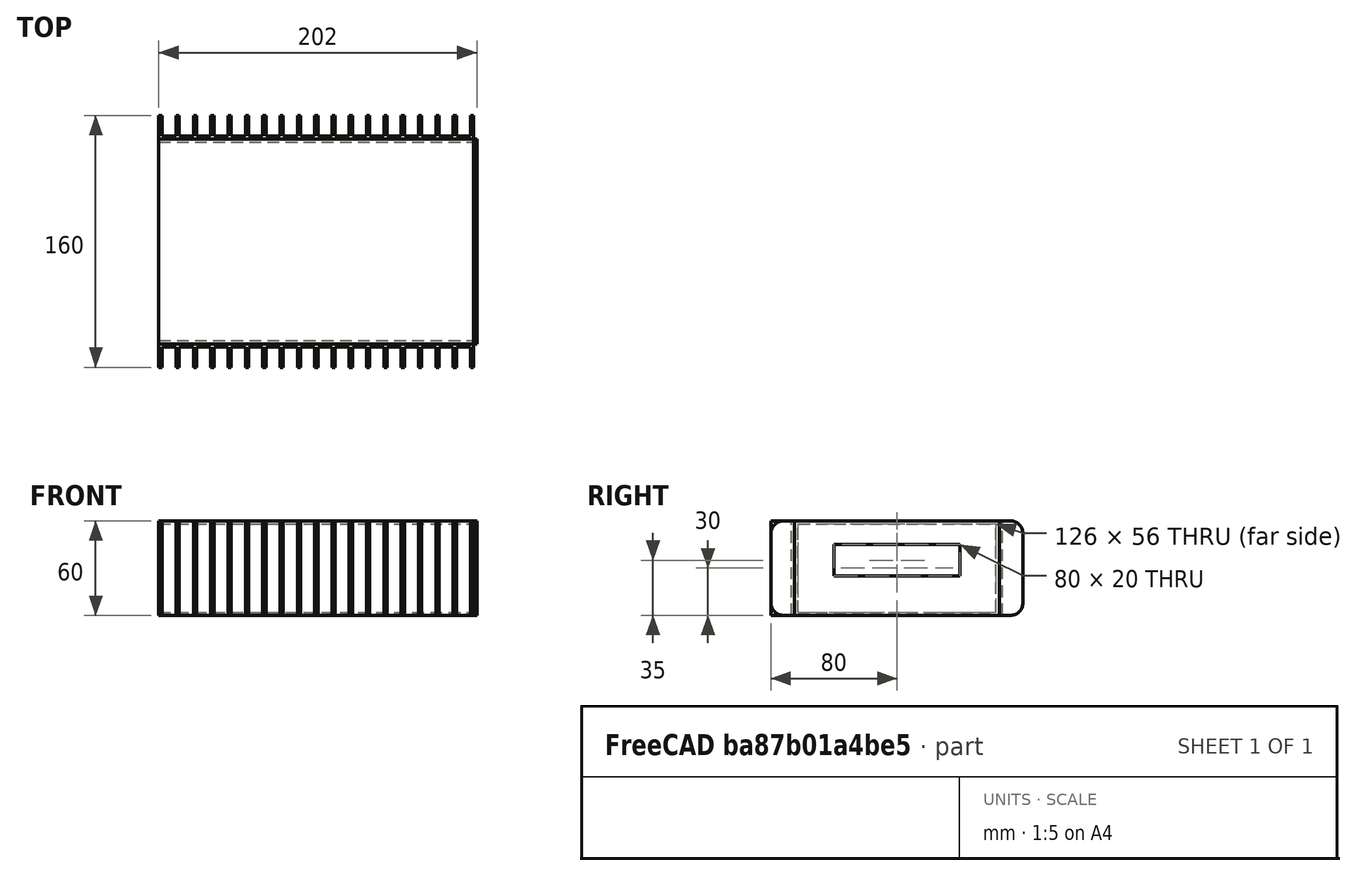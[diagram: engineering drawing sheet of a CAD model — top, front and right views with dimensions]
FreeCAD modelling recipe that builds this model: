
FCSTD DOCUMENT  (FreeCAD 0.16R6710 (Git))
Label: dc_power_supply
License: All rights reserved
LicenseURL: http://en.wikipedia.org/wiki/All_rights_reserved
objects: Part::Box×61, Part::Cut×5, Part::Compound×3, Part::Fillet×1, Part::Mirroring×1
note: 71 computed .brp shape members not serialized (recipe doc carries the construction recipe); baked Part::Feature solids carry a one-line shape summary decoded from their .brp

FEATURE [Part::Box] Box  label="Cube"
  Height = 60
  Length = 200
  Width = 130
FEATURE [Part::Box] Box001  label="Cube001"
  Height = 56
  Length = 200
  Placement = pos=(0,2,2) rot=(0,0,1;0rad)
  Width = 126
FEATURE [Part::Cut] Cut  label="Box"
  Base = -> Box
  Tool = -> Box001
FEATURE [Part::Box] Box002  label="Cube002"
  Height = 60
  Length = 200
  Placement = pos=(0,-15,0) rot=(0,0,1;0rad)
  Width = 15
FEATURE [Part::Box] Box003  label="Cube003"
  Height = 60
  Length = 9
  Placement = pos=(2,-15,0) rot=(0,0,1;0rad)
  Width = 13
FEATURE [Part::Box] Box004  label="Cube004"
  Height = 60
  Length = 9
  Placement = pos=(13,-15,0) rot=(0,0,1;0rad)
  Width = 13
FEATURE [Part::Box] Box005  label="Cube005"
  Height = 60
  Length = 9
  Placement = pos=(24,-15,0) rot=(0,0,1;0rad)
  Width = 13
FEATURE [Part::Box] Box006  label="Cube006"
  Height = 60
  Length = 9
  Placement = pos=(35,-15,0) rot=(0,0,1;0rad)
  Width = 13
FEATURE [Part::Box] Box007  label="Cube007"
  Height = 60
  Length = 9
  Placement = pos=(46,-15,0) rot=(0,0,1;0rad)
  Width = 13
FEATURE [Part::Box] Box008  label="Cube008"
  Height = 60
  Length = 9
  Placement = pos=(57,-15,0) rot=(0,0,1;0rad)
  Width = 13
FEATURE [Part::Box] Box009  label="Cube009"
  Height = 60
  Length = 9
  Placement = pos=(68,-15,0) rot=(0,0,1;0rad)
  Width = 13
FEATURE [Part::Box] Box010  label="Cube010"
  Height = 60
  Length = 9
  Placement = pos=(79,-15,0) rot=(0,0,1;0rad)
  Width = 13
FEATURE [Part::Box] Box011  label="Cube011"
  Height = 60
  Length = 9
  Placement = pos=(90,-15,0) rot=(0,0,1;0rad)
  Width = 13
FEATURE [Part::Box] Box012  label="Cube012"
  Height = 60
  Length = 9
  Placement = pos=(101,-15,0) rot=(0,0,1;0rad)
  Width = 13
FEATURE [Part::Box] Box013  label="Cube013"
  Height = 60
  Length = 9
  Placement = pos=(112,-15,0) rot=(0,0,1;0rad)
  Width = 13
FEATURE [Part::Box] Box014  label="Cube014"
  Height = 60
  Length = 9
  Placement = pos=(123,-15,0) rot=(0,0,1;0rad)
  Width = 13
FEATURE [Part::Box] Box015  label="Cube015"
  Height = 60
  Length = 9
  Placement = pos=(134,-15,0) rot=(0,0,1;0rad)
  Width = 13
FEATURE [Part::Box] Box016  label="Cube016"
  Height = 60
  Length = 9
  Placement = pos=(145,-15,0) rot=(0,0,1;0rad)
  Width = 13
FEATURE [Part::Box] Box017  label="Cube017"
  Height = 60
  Length = 9
  Placement = pos=(156,-15,0) rot=(0,0,1;0rad)
  Width = 13
FEATURE [Part::Box] Box018  label="Cube018"
  Height = 60
  Length = 9
  Placement = pos=(167,-15,0) rot=(0,0,1;0rad)
  Width = 13
FEATURE [Part::Box] Box019  label="Cube019"
  Height = 60
  Length = 9
  Placement = pos=(178,-15,0) rot=(0,0,1;0rad)
  Width = 13
FEATURE [Part::Box] Box020  label="Cube020"
  Height = 60
  Length = 9
  Placement = pos=(189,-15,0) rot=(0,0,1;0rad)
  Width = 13
FEATURE [Part::Compound] Compound
  Links = -> [Box003,Box016,Box004,Box005,Box006,Box007,Box008,Box009,Box010,Box011,Box012,Box013,Box014,Box015,Box017,Box018,Box019,Box020]
FEATURE [Part::Cut] Cut001
  Base = -> Box002
  Tool = -> Compound
FEATURE [Part::Fillet] Fillet  label="Left Heatsink"
  Base = -> Cut001
  Edges = 38 edges r=8: [Edge5,Edge7,Edge10,Edge14,Edge18,Edge22,Edge26,Edge30,Edge34,Edge38,Edge42,Edge46,Edge50,Edge54,Edge58,Edge62,Edge66,Edge70,Edge74,Edge78,Edge85,Edge89,Edge93,Edge97,Edge101,Edge105,Edge109,Edge113,Edge117,Edge121,Edge125,Edge129,Edge133,Edge137,Edge141,Edge145,Edge149,Edge153]
FEATURE [Part::Box] Box021  label="Cube021"
  Height = 60
  Length = 200
  Placement = pos=(0,-15,0) rot=(0,0,1;0rad)
  Width = 15
FEATURE [Part::Box] Box022  label="Cube022"
  Height = 60
  Length = 9
  Placement = pos=(2,-15,0) rot=(0,0,1;0rad)
  Width = 13
FEATURE [Part::Box] Box023  label="Cube023"
  Height = 60
  Length = 9
  Placement = pos=(13,-15,0) rot=(0,0,1;0rad)
  Width = 13
FEATURE [Part::Box] Box024  label="Cube024"
  Height = 60
  Length = 9
  Placement = pos=(24,-15,0) rot=(0,0,1;0rad)
  Width = 13
FEATURE [Part::Box] Box025  label="Cube025"
  Height = 60
  Length = 9
  Placement = pos=(35,-15,0) rot=(0,0,1;0rad)
  Width = 13
FEATURE [Part::Box] Box026  label="Cube026"
  Height = 60
  Length = 9
  Placement = pos=(46,-15,0) rot=(0,0,1;0rad)
  Width = 13
FEATURE [Part::Box] Box027  label="Cube027"
  Height = 60
  Length = 9
  Placement = pos=(57,-15,0) rot=(0,0,1;0rad)
  Width = 13
FEATURE [Part::Box] Box028  label="Cube028"
  Height = 60
  Length = 9
  Placement = pos=(68,-15,0) rot=(0,0,1;0rad)
  Width = 13
FEATURE [Part::Box] Box029  label="Cube029"
  Height = 60
  Length = 9
  Placement = pos=(79,-15,0) rot=(0,0,1;0rad)
  Width = 13
FEATURE [Part::Box] Box030  label="Cube030"
  Height = 60
  Length = 9
  Placement = pos=(90,-15,0) rot=(0,0,1;0rad)
  Width = 13
FEATURE [Part::Box] Box031  label="Cube031"
  Height = 60
  Length = 9
  Placement = pos=(101,-15,0) rot=(0,0,1;0rad)
  Width = 13
FEATURE [Part::Box] Box032  label="Cube032"
  Height = 60
  Length = 9
  Placement = pos=(112,-15,0) rot=(0,0,1;0rad)
  Width = 13
FEATURE [Part::Box] Box033  label="Cube033"
  Height = 60
  Length = 9
  Placement = pos=(123,-15,0) rot=(0,0,1;0rad)
  Width = 13
FEATURE [Part::Box] Box034  label="Cube034"
  Height = 60
  Length = 9
  Placement = pos=(134,-15,0) rot=(0,0,1;0rad)
  Width = 13
FEATURE [Part::Box] Box035  label="Cube035"
  Height = 60
  Length = 9
  Placement = pos=(145,-15,0) rot=(0,0,1;0rad)
  Width = 13
FEATURE [Part::Box] Box036  label="Cube036"
  Height = 60
  Length = 9
  Placement = pos=(156,-15,0) rot=(0,0,1;0rad)
  Width = 13
FEATURE [Part::Box] Box037  label="Cube037"
  Height = 60
  Length = 9
  Placement = pos=(167,-15,0) rot=(0,0,1;0rad)
  Width = 13
FEATURE [Part::Box] Box038  label="Cube038"
  Height = 60
  Length = 9
  Placement = pos=(178,-15,0) rot=(0,0,1;0rad)
  Width = 13
FEATURE [Part::Box] Box039  label="Cube039"
  Height = 60
  Length = 9
  Placement = pos=(189,-15,0) rot=(0,0,1;0rad)
  Width = 13
FEATURE [Part::Compound] Compound001
  Links = -> [Box022,Box035,Box023,Box024,Box025,Box026,Box027,Box028,Box029,Box030,Box031,Box032,Box033,Box034,Box036,Box037,Box038,Box039]
FEATURE [Part::Cut] Cut002
  Base = -> Box021
  Tool = -> Compound001
FEATURE [Part::Box] Box040  label="Cube040"
  Height = 60
  Length = 200
  Placement = pos=(0,-15,0) rot=(0,0,1;0rad)
  Width = 15
FEATURE [Part::Box] Box041  label="Cube041"
  Height = 60
  Length = 9
  Placement = pos=(2,-15,0) rot=(0,0,1;0rad)
  Width = 13
FEATURE [Part::Box] Box042  label="Cube042"
  Height = 60
  Length = 9
  Placement = pos=(13,-15,0) rot=(0,0,1;0rad)
  Width = 13
FEATURE [Part::Box] Box043  label="Cube043"
  Height = 60
  Length = 9
  Placement = pos=(24,-15,0) rot=(0,0,1;0rad)
  Width = 13
FEATURE [Part::Box] Box044  label="Cube044"
  Height = 60
  Length = 9
  Placement = pos=(35,-15,0) rot=(0,0,1;0rad)
  Width = 13
FEATURE [Part::Box] Box045  label="Cube045"
  Height = 60
  Length = 9
  Placement = pos=(46,-15,0) rot=(0,0,1;0rad)
  Width = 13
FEATURE [Part::Box] Box046  label="Cube046"
  Height = 60
  Length = 9
  Placement = pos=(57,-15,0) rot=(0,0,1;0rad)
  Width = 13
FEATURE [Part::Box] Box047  label="Cube047"
  Height = 60
  Length = 9
  Placement = pos=(68,-15,0) rot=(0,0,1;0rad)
  Width = 13
FEATURE [Part::Box] Box048  label="Cube048"
  Height = 60
  Length = 9
  Placement = pos=(79,-15,0) rot=(0,0,1;0rad)
  Width = 13
FEATURE [Part::Box] Box049  label="Cube049"
  Height = 60
  Length = 9
  Placement = pos=(90,-15,0) rot=(0,0,1;0rad)
  Width = 13
FEATURE [Part::Box] Box050  label="Cube050"
  Height = 60
  Length = 9
  Placement = pos=(101,-15,0) rot=(0,0,1;0rad)
  Width = 13
FEATURE [Part::Box] Box051  label="Cube051"
  Height = 60
  Length = 9
  Placement = pos=(112,-15,0) rot=(0,0,1;0rad)
  Width = 13
FEATURE [Part::Box] Box052  label="Cube052"
  Height = 60
  Length = 9
  Placement = pos=(123,-15,0) rot=(0,0,1;0rad)
  Width = 13
FEATURE [Part::Box] Box053  label="Cube053"
  Height = 60
  Length = 9
  Placement = pos=(134,-15,0) rot=(0,0,1;0rad)
  Width = 13
FEATURE [Part::Box] Box054  label="Cube054"
  Height = 60
  Length = 9
  Placement = pos=(145,-15,0) rot=(0,0,1;0rad)
  Width = 13
FEATURE [Part::Box] Box055  label="Cube055"
  Height = 60
  Length = 9
  Placement = pos=(156,-15,0) rot=(0,0,1;0rad)
  Width = 13
FEATURE [Part::Box] Box056  label="Cube056"
  Height = 60
  Length = 9
  Placement = pos=(167,-15,0) rot=(0,0,1;0rad)
  Width = 13
FEATURE [Part::Box] Box057  label="Cube057"
  Height = 60
  Length = 9
  Placement = pos=(178,-15,0) rot=(0,0,1;0rad)
  Width = 13
FEATURE [Part::Box] Box058  label="Cube058"
  Height = 60
  Length = 9
  Placement = pos=(189,-15,0) rot=(0,0,1;0rad)
  Width = 13
FEATURE [Part::Compound] Compound002
  Links = -> [Box041,Box054,Box042,Box043,Box044,Box045,Box046,Box047,Box048,Box049,Box050,Box051,Box052,Box053,Box055,Box056,Box057,Box058]
FEATURE [Part::Cut] Cut003
  Base = -> Box040
  Tool = -> Compound002
FEATURE [Part::Mirroring] Part__Mirroring  label="Right Heatsink"
  Base = (0,0,0)
  Normal = (0,1,0)
  Placement = pos=(0,280,0) rot=(0,0,1;0rad)
FEATURE [Part::Box] Box059  label="Cube059"
  Height = 60
  Length = 2
  Placement = pos=(200,0,0) rot=(0,0,1;0rad)
  Width = 130
FEATURE [Part::Box] Box060  label="Cube060"
  Height = 20
  Length = 2
  Placement = pos=(200,25,25) rot=(0,0,1;0rad)
  Width = 80
FEATURE [Part::Cut] Cut004
  Base = -> Box059
  Tool = -> Box060
